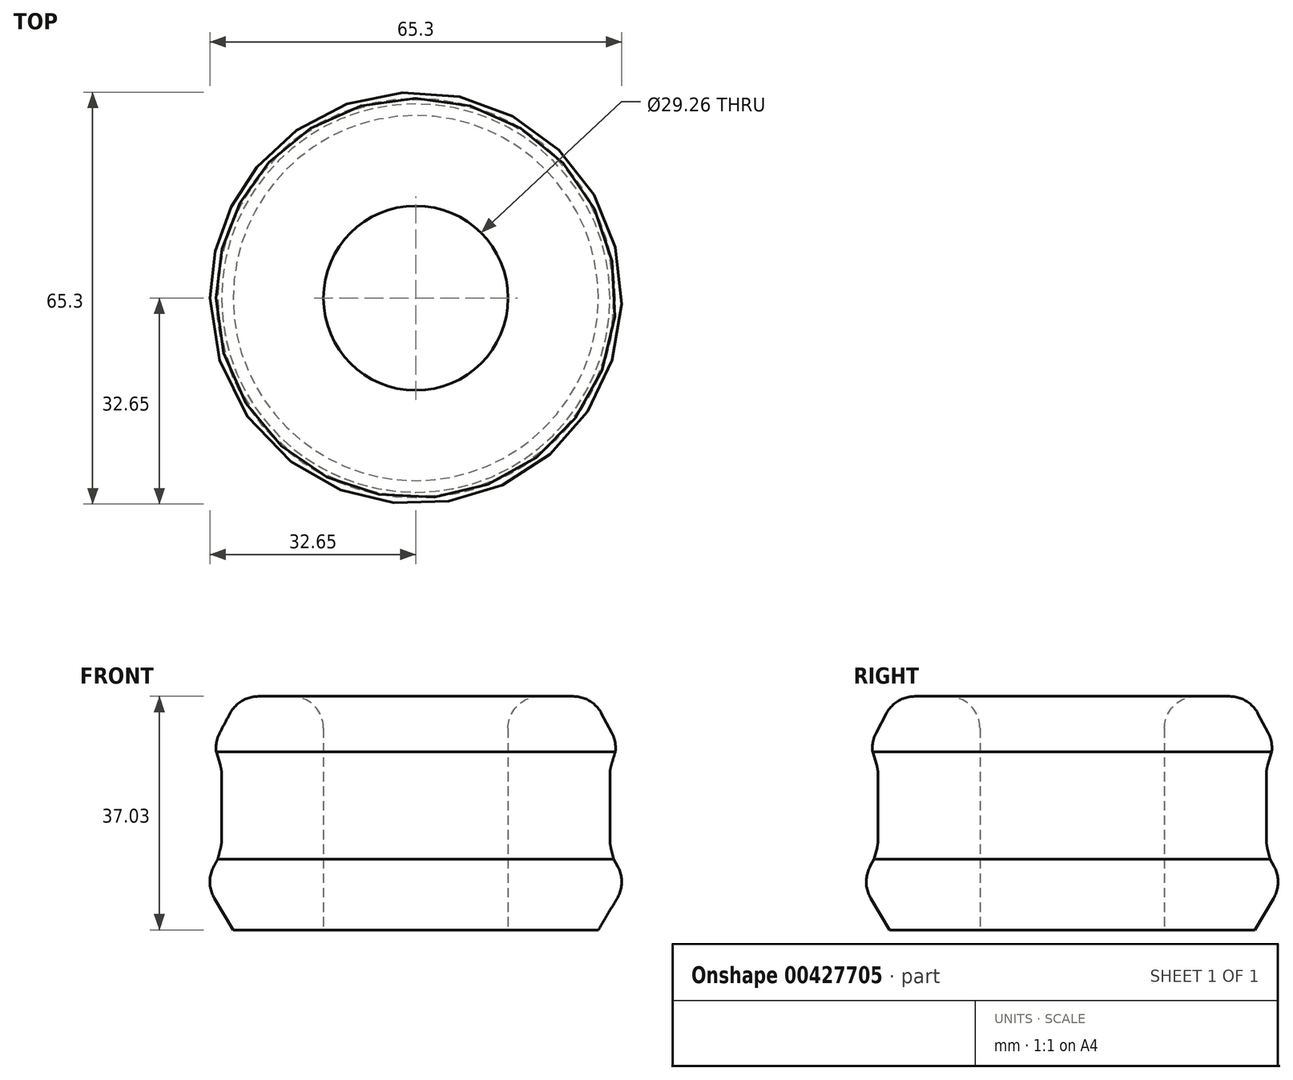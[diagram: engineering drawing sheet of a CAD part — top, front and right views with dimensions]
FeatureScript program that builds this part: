
annotation { "Feature Type Name" : "Feature", "Feature Type Description" : "" }
export const myFeature = defineFeature(function(context is Context, id is Id, definition is map)
    precondition{}
    {
        {
            var Q0;
            Q0=qCreatedBy(makeId("Front.planeOp"),FACE);
            var sketch = newSketch(context, id + "F0", { "sketchPlane" : qUnion([Q0])});
            skLineSegment(sketch, "E0", {"start": v(0, 0) * mm, "end": v(0, 37.03) * mm});
            skLineSegment(sketch, "E1", {"start": v(14.63, 0) * mm, "end": v(14.63, 37.03) * mm});
            skLineSegment(sketch, "E2", {"start": v(14.63, 37.03) * mm, "end": v(37.5, 37.03) * mm});
            skLineSegment(sketch, "E3", {"start": v(37.5, 37.03) * mm, "end": v(30.78, 26.97) * mm});
            skLineSegment(sketch, "E4", {"start": v(30.78, 26.97) * mm, "end": v(30.78, 12.34) * mm});
            skLineSegment(sketch, "E5", {"start": v(30.78, 12.34) * mm, "end": v(37.5, 0) * mm});
            skLineSegment(sketch, "E6", {"start": v(37.5, 0) * mm, "end": v(14.63, 0) * mm});
            skSolve(sketch);
        }
        {
            var Q0;
            Q0=makeQuery(id+"F0.imprint","IMPRINT",FACE,{"disambiguationData":[TD([[makeQuery(id+"F0.imprint","IMPRINT",EDGE,{"derivedFrom":sQuery(id+"F0.wireOp",EDGE,"E1")}),-1.0]])]});
            var Q1;
            Q1=sQuery(id+"F0.wireOp",EDGE,"E0");
            revolve(context, id + "F1", {"entities" : qUnion([Q0]), "axis" : qUnion([Q1]), "revolveType" : RevolveType.FULL});
        }
        {
            var Q0;
            Q0=makeQuery(id+"F1.opRevolve","SWEPT_EDGE",EDGE,{"disambiguationData":[OSD([sQuery(id+"F0.wireOp",EDGE,"E2"),sQuery(id+"F0.wireOp",EDGE,"E3")])]});
            var Q1;
            Q1=makeQuery(id+"F1.opRevolve","SWEPT_EDGE",EDGE,{"disambiguationData":[OSD([sQuery(id+"F0.wireOp",EDGE,"E3"),sQuery(id+"F0.wireOp",EDGE,"E4")])]});
            var Q2;
            Q2=makeQuery(id+"F1.opRevolve","SWEPT_EDGE",EDGE,{"disambiguationData":[OSD([sQuery(id+"F0.wireOp",EDGE,"E4"),sQuery(id+"F0.wireOp",EDGE,"E5")])]});
            var Q3;
            Q3=makeQuery(id+"F1.opRevolve","SWEPT_EDGE",EDGE,{"disambiguationData":[OSD([sQuery(id+"F0.wireOp",EDGE,"E5"),sQuery(id+"F0.wireOp",EDGE,"E6")])]});
            chamfer(context, id + "F2", {"entities" : qUnion([Q0, Q1, Q2, Q3]), "width" : 5.08 * mm, "tangentPropagation" : true});
        }
        {
            var Q0;
            Q0=makeQuery(id+"F1.opRevolve","SWEPT_EDGE",EDGE,{"disambiguationData":[OSD([sQuery(id+"F0.wireOp",EDGE,"E1"),sQuery(id+"F0.wireOp",EDGE,"E2")])]});
            var Q1;
            {var subQ0=sQuery(id+"F0.wireOp",EDGE,"E4");Q1=makeQuery(id+"F2.opChamfer","BLEND_EDGE",EDGE,{"blendedFrom":[makeQuery(id+"F1.opRevolve","SWEPT_EDGE",EDGE,{"disambiguationData":[OSD([sQuery(id+"F0.wireOp",EDGE,"E3"),subQ0])]}),makeQuery(id+"F1.opRevolve","SWEPT_FACE",FACE,{"disambiguationData":[OSD([subQ0])]})],"blendedInto":[makeQuery(id+"F1.opRevolve","SWEPT_FACE",FACE,{"disambiguationData":[OSD([subQ0])]})]});}
            var Q2;
            {var subQ0=sQuery(id+"F0.wireOp",EDGE,"E4");Q2=makeQuery(id+"F2.opChamfer","BLEND_EDGE",EDGE,{"blendedFrom":[makeQuery(id+"F1.opRevolve","SWEPT_EDGE",EDGE,{"disambiguationData":[OSD([subQ0,sQuery(id+"F0.wireOp",EDGE,"E5")])]}),makeQuery(id+"F1.opRevolve","SWEPT_FACE",FACE,{"disambiguationData":[OSD([subQ0])]})],"blendedInto":[makeQuery(id+"F1.opRevolve","SWEPT_FACE",FACE,{"disambiguationData":[OSD([subQ0])]})]});}
            var Q3;
            {var subQ0=sQuery(id+"F0.wireOp",EDGE,"E5");Q3=makeQuery(id+"F2.opChamfer","BLEND_EDGE",EDGE,{"blendedFrom":[makeQuery(id+"F1.opRevolve","SWEPT_EDGE",EDGE,{"disambiguationData":[OSD([subQ0,sQuery(id+"F0.wireOp",EDGE,"E6")])]}),makeQuery(id+"F1.opRevolve","SWEPT_FACE",FACE,{"disambiguationData":[OSD([subQ0])]})],"blendedInto":[makeQuery(id+"F1.opRevolve","SWEPT_FACE",FACE,{"disambiguationData":[OSD([subQ0])]})]});}
            var Q4;
            {var subQ0=sQuery(id+"F0.wireOp",EDGE,"E2");Q4=makeQuery(id+"F2.opChamfer","BLEND_EDGE",EDGE,{"blendedFrom":[makeQuery(id+"F1.opRevolve","SWEPT_EDGE",EDGE,{"disambiguationData":[OSD([subQ0,sQuery(id+"F0.wireOp",EDGE,"E3")])]}),makeQuery(id+"F1.opRevolve","SWEPT_FACE",FACE,{"disambiguationData":[OSD([subQ0])]})],"blendedInto":[makeQuery(id+"F1.opRevolve","SWEPT_FACE",FACE,{"disambiguationData":[OSD([subQ0])]})]});}
            var Q5;
            {var subQ0=sQuery(id+"F0.wireOp",EDGE,"E3");Q5=makeQuery(id+"F2.opChamfer","BLEND_EDGE",EDGE,{"blendedFrom":[makeQuery(id+"F1.opRevolve","SWEPT_EDGE",EDGE,{"disambiguationData":[OSD([sQuery(id+"F0.wireOp",EDGE,"E2"),subQ0])]}),makeQuery(id+"F1.opRevolve","SWEPT_FACE",FACE,{"disambiguationData":[OSD([subQ0])]})],"blendedInto":[makeQuery(id+"F1.opRevolve","SWEPT_FACE",FACE,{"disambiguationData":[OSD([subQ0])]})]});}
            fillet(context, id + "F3", {"entities" : qUnion([Q0, Q1, Q2, Q3, Q4, Q5]), "radius" : 5.08 * mm, "tangentPropagation" : true, "allowEdgeOverflow" : false});
        }
    });
